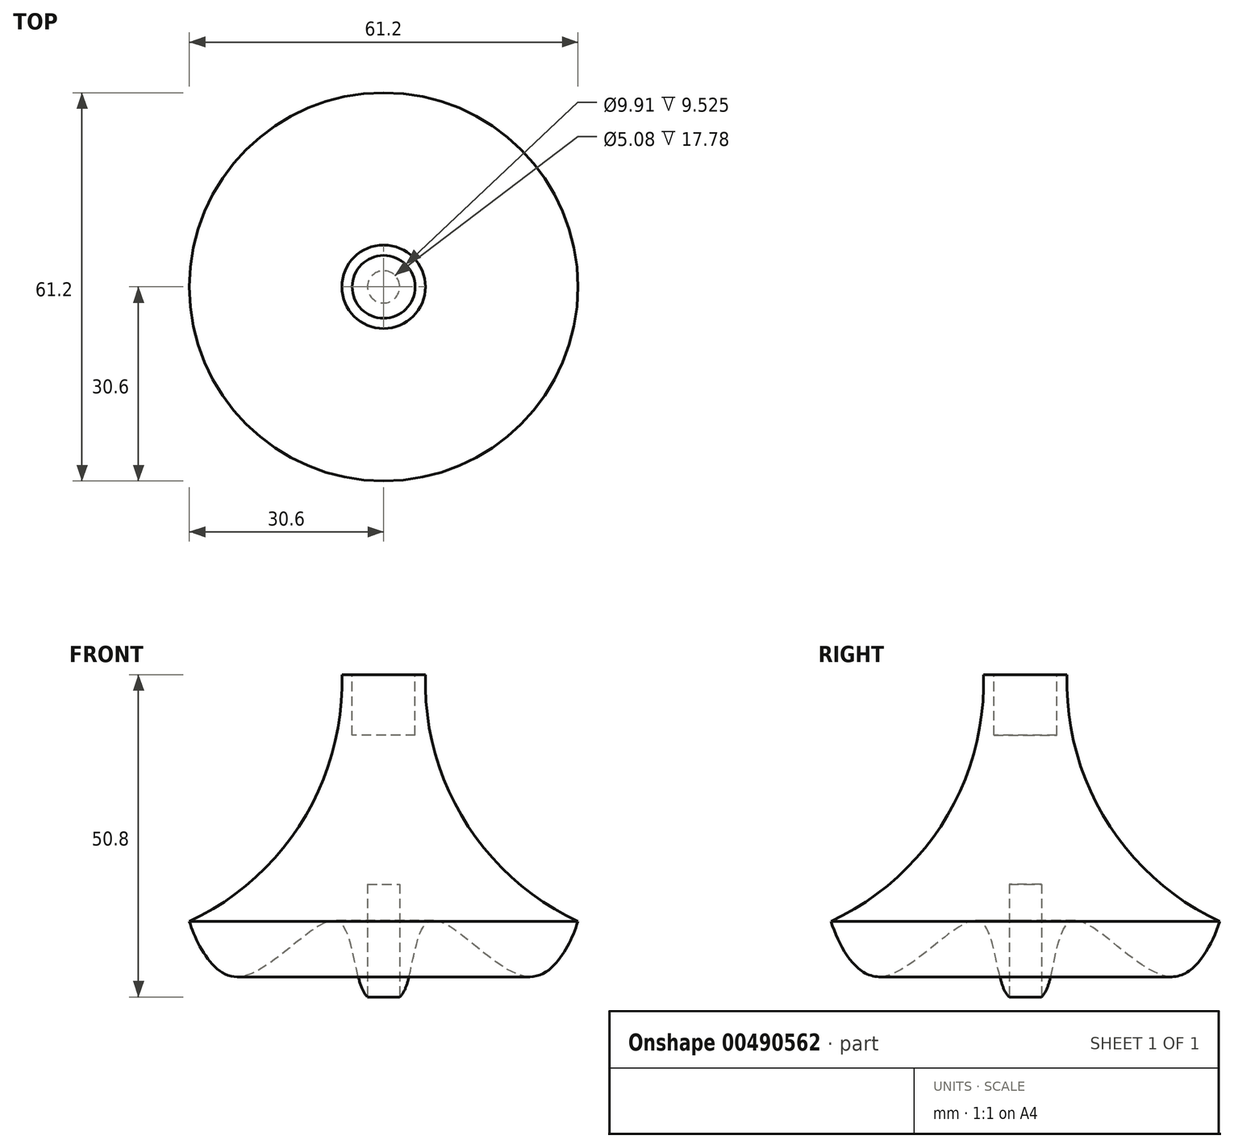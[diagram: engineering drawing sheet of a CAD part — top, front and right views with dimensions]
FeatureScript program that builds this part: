
annotation { "Feature Type Name" : "Feature", "Feature Type Description" : "" }
export const myFeature = defineFeature(function(context is Context, id is Id, definition is map)
    precondition{}
    {
        {
            var Q0;
            Q0=qCreatedBy(makeId("Front.planeOp"),FACE);
            var sketch = newSketch(context, id + "F0", { "sketchPlane" : qUnion([Q0])});
            skLineSegment(sketch, "E0", {"start": v(0, 0) * mm, "end": v(0, 50.8) * mm});
            skLineSegment(sketch, "E1", {"start": v(0, 50.8) * mm, "end": v(6.58, 50.8) * mm});
            skArc(sketch, "E2", {"start": v(6.58, 50.8) * mm, "mid": v(12.77, 27.76) * mm, "end": v(30.6, 11.9) * mm});
            skLineSegment(sketch, "E3", {"start": v(0, 0) * mm, "end": v(2.54, 0) * mm});
            skFitSpline(sketch, "E4", {"points": [v(2.54, 0) * mm, v(7.19, 11.89) * mm, v(22.6, 3.2) * mm, v(30.6, 11.9) * mm], "startDerivative": vector(20.08, 15.97) * mm, "endDerivative": vector(10.92, 34.55) * mm});
            skSolve(sketch);
        }
        {
            var Q0;
            Q0=makeQuery(id+"F0.imprint","IMPRINT",FACE,{"disambiguationData":[TD([[makeQuery(id+"F0.imprint","IMPRINT",EDGE,{"derivedFrom":sQuery(id+"F0.wireOp",EDGE,"E0")}),-1.0]])]});
            var Q1;
            Q1=sQuery(id+"F0.wireOp",EDGE,"E0");
            revolve(context, id + "F1", {"entities" : qUnion([Q0]), "axis" : qUnion([Q1]), "revolveType" : RevolveType.FULL});
        }
        {
            var Q0;
            Q0=makeQuery(id+"F1.opRevolve","SWEPT_FACE",FACE,{"disambiguationData":[OSD([sQuery(id+"F0.wireOp",EDGE,"E1")])]});
            var sketch = newSketch(context, id + "F2", { "sketchPlane" : qUnion([Q0])});
            skCircle(sketch, "E5", {"center": v(0, 0) * mm, "radius": 4.95 * mm});
            skSolve(sketch);
        }
        {
            var Q0;
            Q0=makeQuery(id+"F2.imprint","IMPRINT",FACE,{"disambiguationData":[TD([[makeQuery(id+"F2.imprint","IMPRINT",EDGE,{"derivedFrom":sQuery(id+"F2.wireOp",EDGE,"E5")}),1.0]])]});
            extrude(context, id + "F3", {"entities" : qUnion([Q0]), "operationType" : NewBodyOperationType.REMOVE, "oppositeDirection" : true, "depth" : 9.52 * mm});
        }
        {
            var Q0;
            Q0=makeQuery(id+"F1.opRevolve","SWEPT_FACE",FACE,{"disambiguationData":[OSD([sQuery(id+"F0.wireOp",EDGE,"E3")])]});
            extrude(context, id + "F4", {"entities" : qUnion([Q0]), "operationType" : NewBodyOperationType.REMOVE, "oppositeDirection" : true, "depth" : 17.78 * mm, "offsetDistance" : 25.4 * mm});
        }
    });
